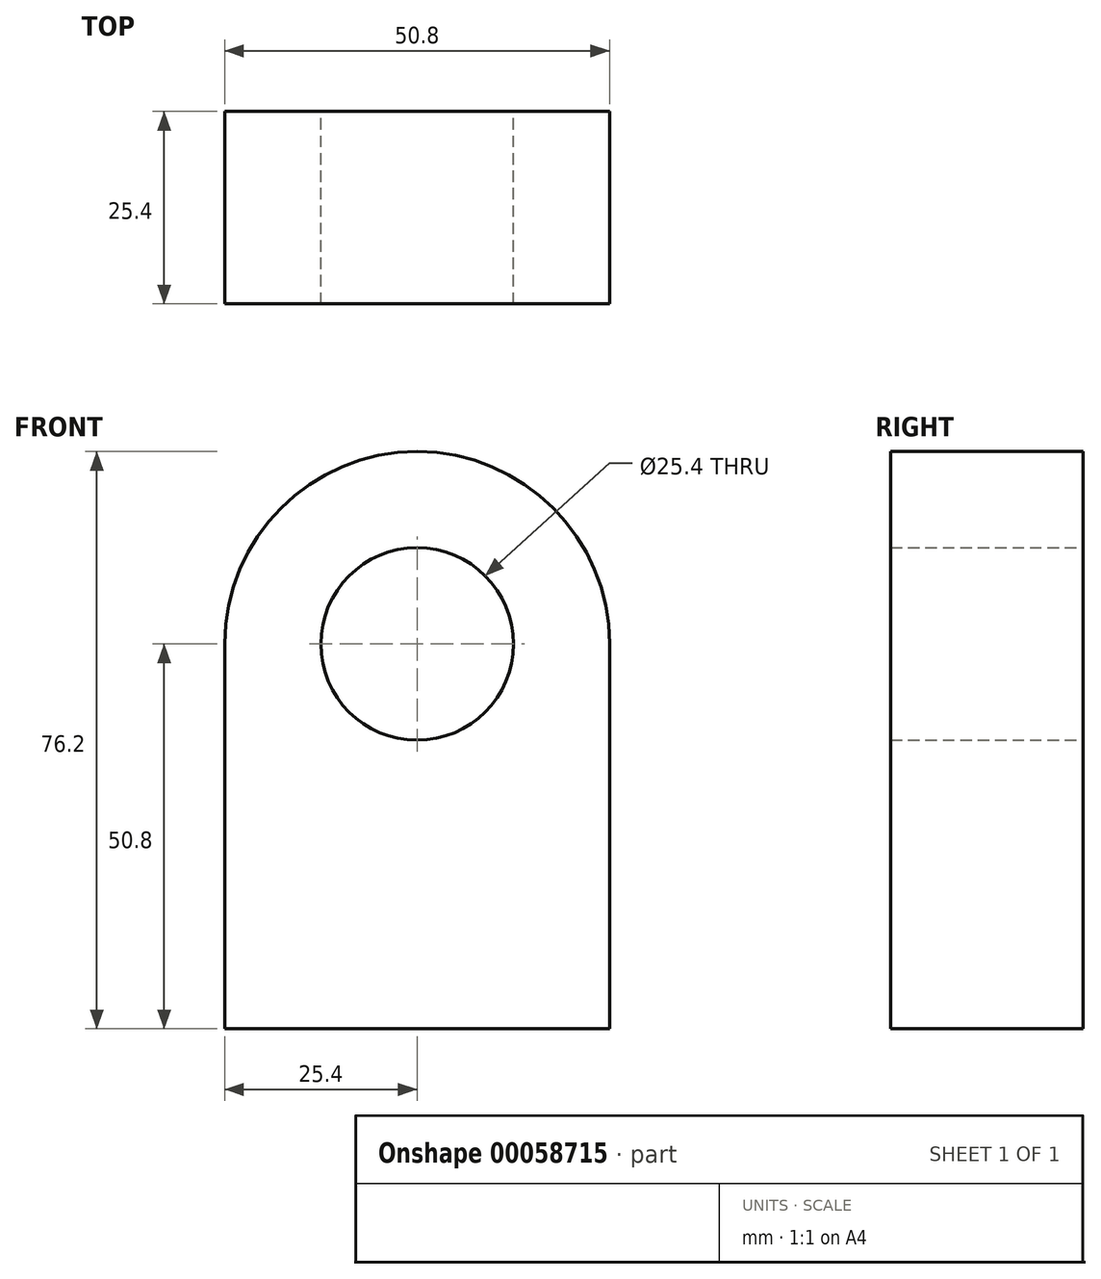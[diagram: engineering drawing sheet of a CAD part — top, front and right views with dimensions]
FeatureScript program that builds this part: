
annotation { "Feature Type Name" : "Feature", "Feature Type Description" : "" }
export const myFeature = defineFeature(function(context is Context, id is Id, definition is map)
    precondition{}
    {
        {
            var Q0;
            Q0=qCreatedBy(makeId("Front.planeOp"),FACE);
            var sketch = newSketch(context, id + "F0", { "sketchPlane" : qUnion([Q0])});
            skCircle(sketch, "E0", {"center": v(0, 0) * mm, "radius": 12.7 * mm});
            skArc(sketch, "E1", {"start": v(25.4, 0) * mm, "mid": v(0, 25.4) * mm, "end": v(-25.4, 0) * mm});
            skLineSegment(sketch, "E2", {"start": v(-25.4, 0) * mm, "end": v(-25.4, -50.8) * mm});
            skLineSegment(sketch, "E3", {"start": v(-25.4, -50.8) * mm, "end": v(25.4, -50.8) * mm});
            skLineSegment(sketch, "E4", {"start": v(25.4, -50.8) * mm, "end": v(25.4, 0) * mm});
            skSolve(sketch);
        }
        {
            var Q0;
            Q0=makeQuery(id+"F0.imprint","IMPRINT",FACE,{"disambiguationData":[TD([[makeQuery(id+"F0.imprint","IMPRINT",EDGE,{"derivedFrom":sQuery(id+"F0.wireOp",EDGE,"E0")}),-1.0]])]});
            extrude(context, id + "F1", {"entities" : qUnion([Q0]), "depth" : 25.4 * mm});
        }
    });
